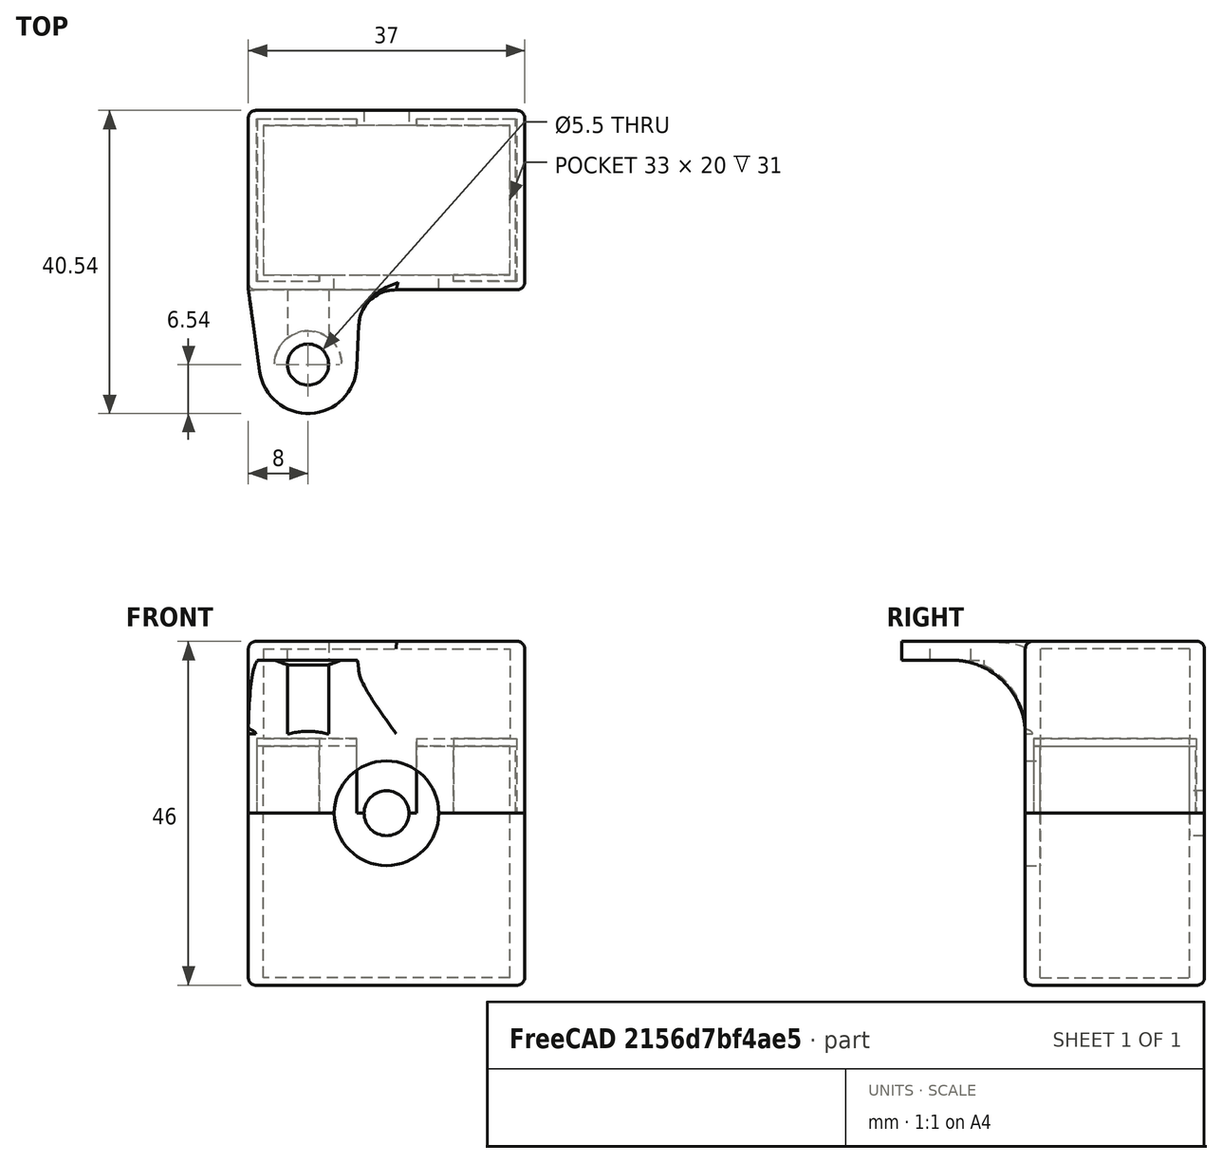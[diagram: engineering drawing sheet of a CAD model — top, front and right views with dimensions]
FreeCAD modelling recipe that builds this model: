
FCSTD DOCUMENT  (FreeCAD 1.1R)
Label: logitech-quickcam-case
License: All rights reserved
LicenseURL: https://en.wikipedia.org/wiki/All_rights_reserved
objects: Sketcher::SketchObject×13, PartDesign::Pad×7, PartDesign::Pocket×6, Part::DatumPlane×5, App::Point×4, PartDesign::Fillet×4, PartDesign::Body×2, App::FeaturePython×1, Assembly::JointGroup×1, Assembly::AssemblyObject×1
note: 79 computed .brp shape members not serialized (recipe doc carries the construction recipe); baked Part::Feature solids carry a one-line shape summary decoded from their .brp

FEATURE [App::Point] Origin001
  Role = Origin
FEATURE [Sketcher::SketchObject] Sketch
  ArcFitTolerance = 1e-06
  AttachmentSupport = -> [Origin]
  ExternalTypes = [0]
  FullyConstrained = true
  MakeInternals = false
  MapMode = 5
  sketch-geometry (12):
    g0: LineSegment StartX=0 StartY=-24 StartZ=0 EndX=0 EndY=0 EndZ=0
    g1: LineSegment StartX=0 StartY=0 StartZ=0 EndX=37 EndY=0 EndZ=0
    g2: LineSegment StartX=37 StartY=0 StartZ=0 EndX=37 EndY=-24 EndZ=0
    g3: LineSegment StartX=37 StartY=-24 StartZ=0 EndX=0 EndY=-24 EndZ=0
    g4: LineSegment StartX=2 StartY=-22 StartZ=0 EndX=2 EndY=-2 EndZ=0
    g5: LineSegment StartX=2 StartY=-2 StartZ=0 EndX=35 EndY=-2 EndZ=0
    g6: LineSegment StartX=35 StartY=-2 StartZ=0 EndX=35 EndY=-22 EndZ=0
    g7: LineSegment StartX=35 StartY=-22 StartZ=0 EndX=2 EndY=-22 EndZ=0
    g8: LineSegment [constr] StartX=0 StartY=-2 StartZ=0 EndX=2 EndY=-2 EndZ=0
    g9: LineSegment [constr] StartX=35 StartY=-2 StartZ=0 EndX=37 EndY=-2 EndZ=0
    g10: LineSegment [constr] StartX=2 StartY=-22 StartZ=0 EndX=2 EndY=-24 EndZ=0
    g11: LineSegment [constr] StartX=2 StartY=-2 StartZ=0 EndX=2 EndY=0 EndZ=0
  constraints (36):
    c: Coincident(g0,g1)
    c: Coincident(g1,g2)
    c: Coincident(g2,g3)
    c: Coincident(g3,g0)
    c: Vertical(g0)
    c: Vertical(g2)
    c: Horizontal(g1)
    c: Horizontal(g3)
    c: PointOnObject(g0,g-2)
    c: PointOnObject(g1,g-1)
    c: Coincident(g4,g5)
    c: Coincident(g5,g6)
    c: Coincident(g6,g7)
    c: Coincident(g7,g4)
    c: Vertical(g4)
    c: Vertical(g6)
    c: Horizontal(g5)
    c: Horizontal(g7)
    c: PointOnObject(g8,g0)
    c: Coincident(g8,g4)
    c: Horizontal(g8)
    c: Coincident(g9,g5)
    c: PointOnObject(g9,g2)
    c: Horizontal(g9)
    c: Equal(g8,g9)
    c: Coincident(g10,g4)
    c: PointOnObject(g10,g3)
    c: Vertical(g10)
    c: Coincident(g11,g4)
    c: PointOnObject(g11,g1)
    c: Perpendicular(g11,g1)
    c: Equal(g11,g10)
    c: Equal(g11,g8)
    c: Distance(g4,g8) = 2
    c: DistanceY(g4,g4) = 20
    c: DistanceX(g7,g7) = 33
FEATURE [PartDesign::Pad] Pad
  Direction = (0,0,1)
  Length = 23
  Length2 = 10
  Profile = -> Sketch
  ReferenceAxis = -> Sketch [N_Axis]
  Refine = true
  SideType = 0
  Suppressed = false
  Type = 0
  Type2 = 0
FEATURE [Sketcher::SketchObject] Sketch001
  ArcFitTolerance = 1e-06
  AttachmentSupport = -> [Origin]
  ExternalTypes = [0]
  FullyConstrained = true
  MakeInternals = false
  MapMode = 5
  sketch-geometry (4):
    g0: LineSegment StartX=0 StartY=0 StartZ=0 EndX=0 EndY=-24 EndZ=0
    g1: LineSegment StartX=0 StartY=-24 StartZ=0 EndX=37 EndY=-24 EndZ=0
    g2: LineSegment StartX=37 StartY=-24 StartZ=0 EndX=37 EndY=0 EndZ=0
    g3: LineSegment StartX=37 StartY=0 StartZ=0 EndX=0 EndY=0 EndZ=0
  constraints (11):
    c: Coincident(g0,g1)
    c: Coincident(g1,g2)
    c: Coincident(g2,g3)
    c: Coincident(g3,g0)
    c: Vertical(g0)
    c: Vertical(g2)
    c: Horizontal(g1)
    c: Horizontal(g3)
    c: Distance(g0,g2) = 37
    c: Distance(g1,g3) = 24
    c: Coincident(g0,g-1)
FEATURE [PartDesign::Pad] Pad001
  BaseFeature = -> Pad
  Direction = (0,0,1)
  Length = 1
  Length2 = 10
  Profile = -> Sketch001
  ReferenceAxis = -> Sketch001 [N_Axis]
  Refine = true
  SideType = 0
  Suppressed = false
  Type = 0
  Type2 = 0
FEATURE [Sketcher::SketchObject] Sketch002
  ArcFitTolerance = 1e-06
  AttachmentSupport = -> [Origin]
  ExternalTypes = [0]
  FullyConstrained = true
  MakeInternals = false
  MapMode = 5
  sketch-geometry (28):
    g0: LineSegment StartX=1.2 StartY=-22.8 StartZ=0 EndX=1.2 EndY=-1.2 EndZ=0
    g1: LineSegment [constr] StartX=1.2 StartY=-1.2 StartZ=0 EndX=35.8 EndY=-1.2 EndZ=0
    g2: LineSegment StartX=35.8 StartY=-1.2 StartZ=0 EndX=35.8 EndY=-22.8 EndZ=0
    g3: LineSegment [constr] StartX=35.8 StartY=-22.8 StartZ=0 EndX=1.2 EndY=-22.8 EndZ=0
    g4: LineSegment StartX=2 StartY=-22 StartZ=0 EndX=2 EndY=-2 EndZ=0
    g5: LineSegment [constr] StartX=2 StartY=-2 StartZ=0 EndX=35 EndY=-2 EndZ=0
    g6: LineSegment StartX=35 StartY=-2 StartZ=0 EndX=35 EndY=-22 EndZ=0
    g7: LineSegment [constr] StartX=35 StartY=-22 StartZ=0 EndX=2 EndY=-22 EndZ=0
    g8: LineSegment [constr] StartX=1.2 StartY=-2 StartZ=0 EndX=2 EndY=-2 EndZ=0
    g9: LineSegment [constr] StartX=35 StartY=-2 StartZ=0 EndX=35.8 EndY=-2 EndZ=0
    g10: LineSegment [constr] StartX=2 StartY=-22 StartZ=0 EndX=2 EndY=-22.8 EndZ=0
    g11: LineSegment [constr] StartX=2 StartY=-2 StartZ=0 EndX=2 EndY=-1.2 EndZ=0
    g12: LineSegment [constr] StartX=1.2 StartY=-1.2 StartZ=0 EndX=0 EndY=-1.2 EndZ=0
    g13: LineSegment [constr] StartX=1.2 StartY=-1.2 StartZ=0 EndX=1.2 EndY=0 EndZ=0
    g14: LineSegment StartX=14.5 StartY=-2 StartZ=0 EndX=14.5 EndY=-1.2 EndZ=0
    g15: LineSegment StartX=22.5 StartY=-1.2 StartZ=0 EndX=22.5 EndY=-2 EndZ=0
    g16: LineSegment StartX=22.5 StartY=-1.2 StartZ=0 EndX=35.8 EndY=-1.2 EndZ=0
    g17: LineSegment StartX=35 StartY=-2 StartZ=0 EndX=22.5 EndY=-2 EndZ=0
    g18: LineSegment StartX=14.5 StartY=-2 StartZ=0 EndX=2 EndY=-2 EndZ=0
    g19: LineSegment StartX=14.5 StartY=-1.2 StartZ=0 EndX=2 EndY=-1.2 EndZ=0
    g20: LineSegment StartX=2 StartY=-1.2 StartZ=0 EndX=1.2 EndY=-1.2 EndZ=0
    g21: LineSegment StartX=2 StartY=-22 StartZ=0 EndX=9.5 EndY=-22 EndZ=0
    g22: LineSegment StartX=9.5 StartY=-22 StartZ=0 EndX=9.5 EndY=-22.8 EndZ=0
    g23: LineSegment StartX=9.5 StartY=-22.8 StartZ=0 EndX=1.2 EndY=-22.8 EndZ=0
    g24: LineSegment StartX=35 StartY=-22 StartZ=0 EndX=27.5 EndY=-22 EndZ=0
    g25: LineSegment StartX=27.5 StartY=-22 StartZ=0 EndX=27.5 EndY=-22.8 EndZ=0
    g26: LineSegment [constr] StartX=9.5 StartY=-22 StartZ=0 EndX=27.5 EndY=-22 EndZ=0
    g27: LineSegment StartX=27.5 StartY=-22.8 StartZ=0 EndX=35.8 EndY=-22.8 EndZ=0
  constraints (78):
    c: Coincident(g0,g1)
    c: Coincident(g1,g2)
    c: Coincident(g2,g3)
    c: Coincident(g3,g0)
    c: Vertical(g0)
    c: Vertical(g2)
    c: Horizontal(g1)
    c: Horizontal(g3)
    c: Coincident(g4,g5)
    c: Coincident(g5,g6)
    c: Coincident(g6,g7)
    c: Coincident(g7,g4)
    c: Vertical(g4)
    c: Vertical(g6)
    c: Horizontal(g5)
    c: Horizontal(g7)
    c: PointOnObject(g8,g0)
    c: Coincident(g8,g4)
    c: Horizontal(g8)
    c: Coincident(g9,g5)
    c: PointOnObject(g9,g2)
    c: Horizontal(g9)
    c: Equal(g8,g9)
    c: Coincident(g10,g4)
    c: PointOnObject(g10,g3)
    c: Vertical(g10)
    c: Coincident(g11,g4)
    c: PointOnObject(g11,g1)
    c: Perpendicular(g11,g1)
    c: Equal(g11,g10)
    c: Equal(g11,g8)
    c: Distance(g4,g8) = 0.8
    c: DistanceY(g4,g4) = 20
    c: DistanceX(g7,g7) = 33
    c: Coincident(g12,g0)
    c: PointOnObject(g12,g-2)
    c: Horizontal(g12)
    c: Coincident(g13,g0)
    c: Vertical(g13)
    c: Equal(g12,g13)
    c: PointOnObject(g13,g-1)
    c: DistanceY(g13,g13) = 1.2
    c: PointOnObject(g14,g5)
    c: PointOnObject(g14,g1)
    c: PointOnObject(g15,g1)
    c: PointOnObject(g15,g5)
    c: Vertical(g15)
    c: Coincident(g16,g15)
    c: Coincident(g16,g1)
    c: Coincident(g17,g5)
    c: Coincident(g17,g15)
    c: Coincident(g18,g14)
    c: Coincident(g18,g4)
    c: Coincident(g19,g14)
    c: Coincident(g19,g11)
    c: Perpendicular(g18,g14)
    c: DistanceX(g14,g15) = 8
    c: Coincident(g20,g11)
    c: Coincident(g20,g0)
    c: Coincident(g21,g4)
    c: Coincident(g21,g22)
    c: Vertical(g22)
    c: Coincident(g22,g23)
    c: Coincident(g23,g0)
    c: Coincident(g24,g6)
    c: Coincident(g24,g25)
    c: Coincident(g26,g21)
    c: Coincident(g26,g24)
    c: Horizontal(g26)
    c: DistanceX(g26,g26) = 18
    c: Perpendicular(g25,g24)
    c: Perpendicular(g6,g24)
    c: Horizontal(g25,g22)
    c: Horizontal(g22,g2)
    c: Equal(g18,g17)
    c: Equal(g21,g24)
    c: Coincident(g27,g25)
    c: Coincident(g27,g2)
FEATURE [Part::DatumPlane] DatumPlane
  AttachmentOffset = pos=(0,0,0) rot=(0,1,0;1.5708rad)
  AttachmentSupport = -> [Pad001]
  MapMode = 7
  Placement = pos=(2,-2,23) rot=(1,0,0;1.5708rad)
FEATURE [Sketcher::SketchObject] Sketch003
  ArcFitTolerance = 1e-06
  AttachmentSupport = -> [DatumPlane]
  ExternalTypes = [0]
  FullyConstrained = true
  MakeInternals = false
  MapMode = 5
  Placement = pos=(2,-2,23) rot=(1,0,0;1.5708rad)
  sketch-geometry (1):
    g0: Circle CenterX=16.5 CenterY=0 CenterZ=0 NormalX=0 NormalY=0 NormalZ=1 AngleXU=0 Radius=3
  constraints (3):
    c: PointOnObject(g0,g-1)
    c: Diameter(g0) = 6
    c: DistanceX(g-1,g0) = 16.5
FEATURE [PartDesign::Pocket] Pocket
  BaseFeature = -> Pad001
  Direction = (0,1,-2e-16)
  Length = 5
  Length2 = 5
  Profile = -> Sketch003
  ReferenceAxis = -> Sketch003 [N_Axis]
  Refine = true
  SideType = 2
  Suppressed = false
  Type = 0
  Type2 = 0
FEATURE [Part::DatumPlane] DatumPlane001
  AttachmentOffset = pos=(0,0,0) rot=(0,1,0;1.5708rad)
  AttachmentSupport = -> [Pad001]
  MapMode = 7
  Placement = pos=(35,-22,23) rot=(0,0.707107,0.707107;3.14159rad)
FEATURE [Sketcher::SketchObject] Sketch005
  ArcFitTolerance = 1e-06
  AttachmentSupport = -> [DatumPlane001]
  ExternalTypes = [0]
  FullyConstrained = true
  MakeInternals = false
  MapMode = 5
  Placement = pos=(35,-22,23) rot=(0,0.707107,0.707107;3.14159rad)
  sketch-geometry (1):
    g0: Circle CenterX=16.5 CenterY=0 CenterZ=0 NormalX=0 NormalY=0 NormalZ=1 AngleXU=0 Radius=7
  constraints (3):
    c: Diameter(g0) = 14
    c: PointOnObject(g0,g-1)
    c: DistanceX(g-1,g0) = 16.5
FEATURE [PartDesign::Pocket] Pocket001
  BaseFeature = -> Pocket
  Direction = (0,-1,2e-16)
  Length = 5
  Length2 = 5
  Profile = -> Sketch005
  ReferenceAxis = -> Sketch005 [N_Axis]
  Refine = true
  SideType = 2
  Suppressed = false
  Type = 0
  Type2 = 0
FEATURE [PartDesign::Pad] Pad002
  BaseFeature = -> Pocket001
  Direction = (0,0,1)
  Length = 32
  Length2 = 10
  Profile = -> Sketch002
  ReferenceAxis = -> Sketch002 [N_Axis]
  Refine = true
  SideType = 0
  Suppressed = false
  Type = 0
  Type2 = 0
FEATURE [App::Point] Origin005
  Role = Origin
FEATURE [Sketcher::SketchObject] Sketch006
  ArcFitTolerance = 1e-06
  AttachmentOffset = pos=(0,0,0) rot=(1,0,0;3.14159rad)
  ExternalTypes = [0]
  FullyConstrained = true
  MakeInternals = false
  MapMode = 5
  Placement = pos=(0,0,23) rot=(0,0,1;0rad)
  sketch-geometry (28):
    g0: LineSegment StartX=1.1 StartY=-22.9 StartZ=0 EndX=1.1 EndY=-1.1 EndZ=0
    g1: LineSegment [constr] StartX=1.1 StartY=-1.1 StartZ=0 EndX=35.9 EndY=-1.1 EndZ=0
    g2: LineSegment StartX=35.9 StartY=-1.1 StartZ=0 EndX=35.9 EndY=-22.9 EndZ=0
    g3: LineSegment [constr] StartX=35.9 StartY=-22.9 StartZ=0 EndX=1.1 EndY=-22.9 EndZ=0
    g4: LineSegment StartX=2 StartY=-22 StartZ=0 EndX=2 EndY=-2 EndZ=0
    g5: LineSegment [constr] StartX=2 StartY=-2 StartZ=0 EndX=35 EndY=-2 EndZ=0
    g6: LineSegment StartX=35 StartY=-2 StartZ=0 EndX=35 EndY=-22 EndZ=0
    g7: LineSegment [constr] StartX=35 StartY=-22 StartZ=0 EndX=2 EndY=-22 EndZ=0
    g8: LineSegment [constr] StartX=1.1 StartY=-2 StartZ=0 EndX=2 EndY=-2 EndZ=0
    g9: LineSegment [constr] StartX=35 StartY=-2 StartZ=0 EndX=35.9 EndY=-2 EndZ=0
    g10: LineSegment [constr] StartX=2 StartY=-22 StartZ=0 EndX=2 EndY=-22.9 EndZ=0
    g11: LineSegment [constr] StartX=2 StartY=-2 StartZ=0 EndX=2 EndY=-1.1 EndZ=0
    g12: LineSegment [constr] StartX=1.1 StartY=-1.1 StartZ=0 EndX=0 EndY=-1.1 EndZ=0
    g13: LineSegment [constr] StartX=1.1 StartY=-1.1 StartZ=0 EndX=1.1 EndY=0 EndZ=0
    g14: LineSegment StartX=14.5 StartY=-2 StartZ=0 EndX=14.5 EndY=-1.1 EndZ=0
    g15: LineSegment StartX=22.5 StartY=-1.1 StartZ=0 EndX=22.5 EndY=-2 EndZ=0
    g16: LineSegment StartX=22.5 StartY=-1.1 StartZ=0 EndX=35.9 EndY=-1.1 EndZ=0
    g17: LineSegment StartX=35 StartY=-2 StartZ=0 EndX=22.5 EndY=-2 EndZ=0
    g18: LineSegment StartX=14.5 StartY=-2 StartZ=0 EndX=2 EndY=-2 EndZ=0
    g19: LineSegment StartX=14.5 StartY=-1.1 StartZ=0 EndX=2 EndY=-1.1 EndZ=0
    g20: LineSegment StartX=2 StartY=-1.1 StartZ=0 EndX=1.1 EndY=-1.1 EndZ=0
    g21: LineSegment StartX=2 StartY=-22 StartZ=0 EndX=9.5 EndY=-22 EndZ=0
    g22: LineSegment StartX=9.5 StartY=-22 StartZ=0 EndX=9.5 EndY=-22.9 EndZ=0
    g23: LineSegment StartX=9.5 StartY=-22.9 StartZ=0 EndX=1.1 EndY=-22.9 EndZ=0
    g24: LineSegment StartX=35 StartY=-22 StartZ=0 EndX=27.5 EndY=-22 EndZ=0
    g25: LineSegment StartX=27.5 StartY=-22 StartZ=0 EndX=27.5 EndY=-22.9 EndZ=0
    g26: LineSegment [constr] StartX=9.5 StartY=-22 StartZ=0 EndX=27.5 EndY=-22 EndZ=0
    g27: LineSegment StartX=27.5 StartY=-22.9 StartZ=0 EndX=35.9 EndY=-22.9 EndZ=0
  constraints (78):
    c: Coincident(g0,g1)
    c: Coincident(g1,g2)
    c: Coincident(g2,g3)
    c: Coincident(g3,g0)
    c: Vertical(g0)
    c: Vertical(g2)
    c: Horizontal(g1)
    c: Horizontal(g3)
    c: Coincident(g4,g5)
    c: Coincident(g5,g6)
    c: Coincident(g6,g7)
    c: Coincident(g7,g4)
    c: Vertical(g4)
    c: Vertical(g6)
    c: Horizontal(g5)
    c: Horizontal(g7)
    c: PointOnObject(g8,g0)
    c: Coincident(g8,g4)
    c: Horizontal(g8)
    c: Coincident(g9,g5)
    c: PointOnObject(g9,g2)
    c: Horizontal(g9)
    c: Equal(g8,g9)
    c: Coincident(g10,g4)
    c: PointOnObject(g10,g3)
    c: Vertical(g10)
    c: Coincident(g11,g4)
    c: PointOnObject(g11,g1)
    c: Perpendicular(g11,g1)
    c: Equal(g11,g10)
    c: Equal(g11,g8)
    c: Distance(g4,g8) = 0.9
    c: DistanceY(g4,g4) = 20
    c: DistanceX(g7,g7) = 33
    c: Coincident(g12,g0)
    c: PointOnObject(g12,g-2)
    c: Horizontal(g12)
    c: Coincident(g13,g0)
    c: Vertical(g13)
    c: Equal(g12,g13)
    c: PointOnObject(g13,g-1)
    c: DistanceY(g13,g13) = 1.1
    c: PointOnObject(g14,g5)
    c: PointOnObject(g14,g1)
    c: PointOnObject(g15,g1)
    c: PointOnObject(g15,g5)
    c: Vertical(g15)
    c: Coincident(g16,g15)
    c: Coincident(g16,g1)
    c: Coincident(g17,g5)
    c: Coincident(g17,g15)
    c: Coincident(g18,g14)
    c: Coincident(g18,g4)
    c: Coincident(g19,g14)
    c: Coincident(g19,g11)
    c: Perpendicular(g18,g14)
    c: DistanceX(g14,g15) = 8
    c: Coincident(g20,g11)
    c: Coincident(g20,g0)
    c: Coincident(g21,g4)
    c: Coincident(g21,g22)
    c: Vertical(g22)
    c: Coincident(g22,g23)
    c: Coincident(g23,g0)
    c: Coincident(g24,g6)
    c: Coincident(g24,g25)
    c: Coincident(g26,g21)
    c: Coincident(g26,g24)
    c: Horizontal(g26)
    c: DistanceX(g26,g26) = 18
    c: Perpendicular(g25,g24)
    c: Perpendicular(g6,g24)
    c: Horizontal(g25,g22)
    c: Horizontal(g22,g2)
    c: Equal(g18,g17)
    c: Equal(g21,g24)
    c: Coincident(g27,g25)
    c: Coincident(g27,g2)
FEATURE [App::Point] Origin007
  Role = Origin
FEATURE [Sketcher::SketchObject] Sketch007
  ArcFitTolerance = 1e-06
  AttachmentSupport = -> [Origin006]
  ExternalTypes = [0]
  FullyConstrained = true
  MakeInternals = false
  MapMode = 5
  sketch-geometry (12):
    g0: LineSegment StartX=0 StartY=-24 StartZ=0 EndX=0 EndY=0 EndZ=0
    g1: LineSegment StartX=0 StartY=0 StartZ=0 EndX=37 EndY=0 EndZ=0
    g2: LineSegment StartX=37 StartY=0 StartZ=0 EndX=37 EndY=-24 EndZ=0
    g3: LineSegment StartX=37 StartY=-24 StartZ=0 EndX=0 EndY=-24 EndZ=0
    g4: LineSegment StartX=2 StartY=-22 StartZ=0 EndX=2 EndY=-2 EndZ=0
    g5: LineSegment StartX=2 StartY=-2 StartZ=0 EndX=35 EndY=-2 EndZ=0
    g6: LineSegment StartX=35 StartY=-2 StartZ=0 EndX=35 EndY=-22 EndZ=0
    g7: LineSegment StartX=35 StartY=-22 StartZ=0 EndX=2 EndY=-22 EndZ=0
    g8: LineSegment [constr] StartX=0 StartY=-2 StartZ=0 EndX=2 EndY=-2 EndZ=0
    g9: LineSegment [constr] StartX=35 StartY=-2 StartZ=0 EndX=37 EndY=-2 EndZ=0
    g10: LineSegment [constr] StartX=2 StartY=-22 StartZ=0 EndX=2 EndY=-24 EndZ=0
    g11: LineSegment [constr] StartX=2 StartY=-2 StartZ=0 EndX=2 EndY=0 EndZ=0
  constraints (36):
    c: Coincident(g0,g1)
    c: Coincident(g1,g2)
    c: Coincident(g2,g3)
    c: Coincident(g3,g0)
    c: Vertical(g0)
    c: Vertical(g2)
    c: Horizontal(g1)
    c: Horizontal(g3)
    c: PointOnObject(g0,g-2)
    c: PointOnObject(g1,g-1)
    c: Coincident(g4,g5)
    c: Coincident(g5,g6)
    c: Coincident(g6,g7)
    c: Coincident(g7,g4)
    c: Vertical(g4)
    c: Vertical(g6)
    c: Horizontal(g5)
    c: Horizontal(g7)
    c: PointOnObject(g8,g0)
    c: Coincident(g8,g4)
    c: Horizontal(g8)
    c: Coincident(g9,g5)
    c: PointOnObject(g9,g2)
    c: Horizontal(g9)
    c: Equal(g8,g9)
    c: Coincident(g10,g4)
    c: PointOnObject(g10,g3)
    c: Vertical(g10)
    c: Coincident(g11,g4)
    c: PointOnObject(g11,g1)
    c: Perpendicular(g11,g1)
    c: Equal(g11,g10)
    c: Equal(g11,g8)
    c: Distance(g4,g8) = 2
    c: DistanceY(g4,g4) = 20
    c: DistanceX(g7,g7) = 33
FEATURE [PartDesign::Pad] Pad003
  Direction = (0,0,1)
  Length = 23
  Length2 = 10
  Profile = -> Sketch007
  ReferenceAxis = -> Sketch007 [N_Axis]
  Refine = true
  SideType = 0
  Suppressed = false
  Type = 0
  Type2 = 0
FEATURE [Sketcher::SketchObject] Sketch008
  ArcFitTolerance = 1e-06
  AttachmentSupport = -> [Origin006]
  ExternalTypes = [0]
  FullyConstrained = true
  MakeInternals = false
  MapMode = 5
  sketch-geometry (4):
    g0: LineSegment StartX=0 StartY=0 StartZ=0 EndX=0 EndY=-24 EndZ=0
    g1: LineSegment StartX=0 StartY=-24 StartZ=0 EndX=37 EndY=-24 EndZ=0
    g2: LineSegment StartX=37 StartY=-24 StartZ=0 EndX=37 EndY=0 EndZ=0
    g3: LineSegment StartX=37 StartY=0 StartZ=0 EndX=0 EndY=0 EndZ=0
  constraints (11):
    c: Coincident(g0,g1)
    c: Coincident(g1,g2)
    c: Coincident(g2,g3)
    c: Coincident(g3,g0)
    c: Vertical(g0)
    c: Vertical(g2)
    c: Horizontal(g1)
    c: Horizontal(g3)
    c: Distance(g0,g2) = 37
    c: Distance(g1,g3) = 24
    c: Coincident(g0,g-1)
FEATURE [PartDesign::Pad] Pad004
  BaseFeature = -> Pad003
  Direction = (0,0,1)
  Length = 1
  Length2 = 10
  Profile = -> Sketch008
  ReferenceAxis = -> Sketch008 [N_Axis]
  Refine = true
  SideType = 0
  Suppressed = false
  Type = 0
  Type2 = 0
FEATURE [Part::DatumPlane] DatumPlane002
  AttachmentOffset = pos=(0,0,0) rot=(0,1,0;1.5708rad)
  AttachmentSupport = -> [Pad004]
  MapMode = 7
  Placement = pos=(2,-2,23) rot=(1,0,0;1.5708rad)
FEATURE [Part::DatumPlane] DatumPlane003
  AttachmentOffset = pos=(0,0,0) rot=(0,1,0;1.5708rad)
  AttachmentSupport = -> [Pad004]
  MapMode = 7
  Placement = pos=(35,-22,23) rot=(0,0.707107,0.707107;3.14159rad)
FEATURE [Sketcher::SketchObject] Sketch009
  ArcFitTolerance = 1e-06
  AttachmentSupport = -> [Origin006]
  ExternalTypes = [0]
  FullyConstrained = true
  MakeInternals = false
  MapMode = 5
  sketch-geometry (28):
    g0: LineSegment StartX=1.2 StartY=-22.8 StartZ=0 EndX=1.2 EndY=-1.2 EndZ=0
    g1: LineSegment [constr] StartX=1.2 StartY=-1.2 StartZ=0 EndX=35.8 EndY=-1.2 EndZ=0
    g2: LineSegment StartX=35.8 StartY=-1.2 StartZ=0 EndX=35.8 EndY=-22.8 EndZ=0
    g3: LineSegment [constr] StartX=35.8 StartY=-22.8 StartZ=0 EndX=1.2 EndY=-22.8 EndZ=0
    g4: LineSegment StartX=2 StartY=-22 StartZ=0 EndX=2 EndY=-2 EndZ=0
    g5: LineSegment [constr] StartX=2 StartY=-2 StartZ=0 EndX=35 EndY=-2 EndZ=0
    g6: LineSegment StartX=35 StartY=-2 StartZ=0 EndX=35 EndY=-22 EndZ=0
    g7: LineSegment [constr] StartX=35 StartY=-22 StartZ=0 EndX=2 EndY=-22 EndZ=0
    g8: LineSegment [constr] StartX=1.2 StartY=-2 StartZ=0 EndX=2 EndY=-2 EndZ=0
    g9: LineSegment [constr] StartX=35 StartY=-2 StartZ=0 EndX=35.8 EndY=-2 EndZ=0
    g10: LineSegment [constr] StartX=2 StartY=-22 StartZ=0 EndX=2 EndY=-22.8 EndZ=0
    g11: LineSegment [constr] StartX=2 StartY=-2 StartZ=0 EndX=2 EndY=-1.2 EndZ=0
    g12: LineSegment [constr] StartX=1.2 StartY=-1.2 StartZ=0 EndX=0 EndY=-1.2 EndZ=0
    g13: LineSegment [constr] StartX=1.2 StartY=-1.2 StartZ=0 EndX=1.2 EndY=0 EndZ=0
    g14: LineSegment StartX=14.5 StartY=-2 StartZ=0 EndX=14.5 EndY=-1.2 EndZ=0
    g15: LineSegment StartX=22.5 StartY=-1.2 StartZ=0 EndX=22.5 EndY=-2 EndZ=0
    g16: LineSegment StartX=22.5 StartY=-1.2 StartZ=0 EndX=35.8 EndY=-1.2 EndZ=0
    g17: LineSegment StartX=35 StartY=-2 StartZ=0 EndX=22.5 EndY=-2 EndZ=0
    g18: LineSegment StartX=14.5 StartY=-2 StartZ=0 EndX=2 EndY=-2 EndZ=0
    g19: LineSegment StartX=14.5 StartY=-1.2 StartZ=0 EndX=2 EndY=-1.2 EndZ=0
    g20: LineSegment StartX=2 StartY=-1.2 StartZ=0 EndX=1.2 EndY=-1.2 EndZ=0
    g21: LineSegment StartX=2 StartY=-22 StartZ=0 EndX=9.5 EndY=-22 EndZ=0
    g22: LineSegment StartX=9.5 StartY=-22 StartZ=0 EndX=9.5 EndY=-22.8 EndZ=0
    g23: LineSegment StartX=9.5 StartY=-22.8 StartZ=0 EndX=1.2 EndY=-22.8 EndZ=0
    g24: LineSegment StartX=35 StartY=-22 StartZ=0 EndX=27.5 EndY=-22 EndZ=0
    g25: LineSegment StartX=27.5 StartY=-22 StartZ=0 EndX=27.5 EndY=-22.8 EndZ=0
    g26: LineSegment [constr] StartX=9.5 StartY=-22 StartZ=0 EndX=27.5 EndY=-22 EndZ=0
    g27: LineSegment StartX=27.5 StartY=-22.8 StartZ=0 EndX=35.8 EndY=-22.8 EndZ=0
  constraints (78):
    c: Coincident(g0,g1)
    c: Coincident(g1,g2)
    c: Coincident(g2,g3)
    c: Coincident(g3,g0)
    c: Vertical(g0)
    c: Vertical(g2)
    c: Horizontal(g1)
    c: Horizontal(g3)
    c: Coincident(g4,g5)
    c: Coincident(g5,g6)
    c: Coincident(g6,g7)
    c: Coincident(g7,g4)
    c: Vertical(g4)
    c: Vertical(g6)
    c: Horizontal(g5)
    c: Horizontal(g7)
    c: PointOnObject(g8,g0)
    c: Coincident(g8,g4)
    c: Horizontal(g8)
    c: Coincident(g9,g5)
    c: PointOnObject(g9,g2)
    c: Horizontal(g9)
    c: Equal(g8,g9)
    c: Coincident(g10,g4)
    c: PointOnObject(g10,g3)
    c: Vertical(g10)
    c: Coincident(g11,g4)
    c: PointOnObject(g11,g1)
    c: Perpendicular(g11,g1)
    c: Equal(g11,g10)
    c: Equal(g11,g8)
    c: Distance(g4,g8) = 0.8
    c: DistanceY(g4,g4) = 20
    c: DistanceX(g7,g7) = 33
    c: Coincident(g12,g0)
    c: PointOnObject(g12,g-2)
    c: Horizontal(g12)
    c: Coincident(g13,g0)
    c: Vertical(g13)
    c: Equal(g12,g13)
    c: PointOnObject(g13,g-1)
    c: DistanceY(g13,g13) = 1.2
    c: PointOnObject(g14,g5)
    c: PointOnObject(g14,g1)
    c: PointOnObject(g15,g1)
    c: PointOnObject(g15,g5)
    c: Vertical(g15)
    c: Coincident(g16,g15)
    c: Coincident(g16,g1)
    c: Coincident(g17,g5)
    c: Coincident(g17,g15)
    c: Coincident(g18,g14)
    c: Coincident(g18,g4)
    c: Coincident(g19,g14)
    c: Coincident(g19,g11)
    c: Perpendicular(g18,g14)
    c: DistanceX(g14,g15) = 8
    c: Coincident(g20,g11)
    c: Coincident(g20,g0)
    c: Coincident(g21,g4)
    c: Coincident(g21,g22)
    c: Vertical(g22)
    c: Coincident(g22,g23)
    c: Coincident(g23,g0)
    c: Coincident(g24,g6)
    c: Coincident(g24,g25)
    c: Coincident(g26,g21)
    c: Coincident(g26,g24)
    c: Horizontal(g26)
    c: DistanceX(g26,g26) = 18
    c: Perpendicular(g25,g24)
    c: Perpendicular(g6,g24)
    c: Horizontal(g25,g22)
    c: Horizontal(g22,g2)
    c: Equal(g18,g17)
    c: Equal(g21,g24)
    c: Coincident(g27,g25)
    c: Coincident(g27,g2)
FEATURE [Sketcher::SketchObject] Sketch010
  ArcFitTolerance = 1e-06
  AttachmentSupport = -> [DatumPlane002]
  ExternalTypes = [0]
  FullyConstrained = true
  MakeInternals = false
  MapMode = 5
  Placement = pos=(2,-2,23) rot=(1,0,0;1.5708rad)
  sketch-geometry (1):
    g0: Circle CenterX=16.5 CenterY=0 CenterZ=0 NormalX=0 NormalY=0 NormalZ=1 AngleXU=0 Radius=3
  constraints (3):
    c: PointOnObject(g0,g-1)
    c: Diameter(g0) = 6
    c: DistanceX(g-1,g0) = 16.5
FEATURE [PartDesign::Pocket] Pocket002
  BaseFeature = -> Pad004
  Direction = (0,1,-2e-16)
  Length = 5
  Length2 = 5
  Profile = -> Sketch010
  ReferenceAxis = -> Sketch010 [N_Axis]
  Refine = true
  SideType = 2
  Suppressed = false
  Type = 0
  Type2 = 0
FEATURE [Sketcher::SketchObject] Sketch011
  ArcFitTolerance = 1e-06
  AttachmentSupport = -> [DatumPlane003]
  ExternalTypes = [0]
  FullyConstrained = true
  MakeInternals = false
  MapMode = 5
  Placement = pos=(35,-22,23) rot=(0,0.707107,0.707107;3.14159rad)
  sketch-geometry (1):
    g0: Circle CenterX=16.5 CenterY=0 CenterZ=0 NormalX=0 NormalY=0 NormalZ=1 AngleXU=0 Radius=7
  constraints (3):
    c: Diameter(g0) = 14
    c: PointOnObject(g0,g-1)
    c: DistanceX(g-1,g0) = 16.5
FEATURE [PartDesign::Pocket] Pocket003
  BaseFeature = -> Pocket002
  Direction = (0,-1,2e-16)
  Length = 5
  Length2 = 5
  Profile = -> Sketch011
  ReferenceAxis = -> Sketch011 [N_Axis]
  Refine = true
  SideType = 2
  Suppressed = false
  Type = 0
  Type2 = 0
FEATURE [PartDesign::Pad] Pad005
  BaseFeature = -> Pocket003
  Direction = (0,0,1)
  Length = 27
  Length2 = 10
  Profile = -> Sketch009
  ReferenceAxis = -> Sketch009 [N_Axis]
  Refine = true
  SideType = 0
  Suppressed = false
  Type = 0
  Type2 = 0
FEATURE [PartDesign::Pocket] Pocket004
  BaseFeature = -> Pad005
  Direction = (0,0,-1)
  Length = 10
  Length2 = 5
  Profile = -> Sketch006
  ReferenceAxis = -> Sketch006 [N_Axis]
  Refine = true
  SideType = 2
  Suppressed = false
  Type = 0
  Type2 = 0
FEATURE [App::Point] Origin009
  Role = Origin
FEATURE [App::FeaturePython] Joint  label="Fixed"  # Assembly joint (typed FeaturePython)
  AngleMax = 0
  AngleMin = 0
  Detach1 = false
  Detach2 = false
  Distance = 0
  Distance2 = 0
  EnableAngleMax = false
  EnableAngleMin = false
  EnableLengthMax = false
  EnableLengthMin = false
  JointType = 0 (Fixed)
  LengthMax = 0
  LengthMin = 0
  Placement1 = pos=(31.25,-22,18) rot=(-0.707107,0,0.707107;3.14159rad)
  Placement2 = pos=(0,-12,23) rot=(0.57735,0.57735,0.57735;4.18879rad)
  Reference1 = -> Assembly [Body001.?Edge92,Body001.?Edge92]
  Reference2 = -> Assembly [Body.?Edge14,Body.?Edge14]
  Suppressed = false
FEATURE [Assembly::JointGroup] Joints
  Group = -> [Joint]
FEATURE [PartDesign::Fillet] Fillet002
  Base = -> Pad002 [Edge29,Edge27,Edge28,Edge25,Edge49,Edge46,Edge26,Edge48]
  BaseFeature = -> Pad002
  Radius = 0.999
  Refine = true
  SupportTransform = false
  Suppressed = false
  UseAllEdges = false
FEATURE [PartDesign::Body] Body  label="free-side"
  AllowCompound = false
  Group = -> [Sketch,Pad,Sketch001,Pad001,Sketch003,Pocket,Sketch002,Sketch005,Pocket001,Pad002,DatumPlane,DatumPlane001,Fillet002]
  Origin = -> Origin
  Tip = -> Fillet002
FEATURE [Part::DatumPlane] DatumPlane005
  AttachmentOffset = pos=(0,0,0) rot=(-0.57735,0.57735,0.57735;2.0944rad)
  AttachmentSupport = -> [Pocket004]
  MapMode = 7
  Placement = pos=(37,-24,0) rot=(0,0,1;3.14159rad)
FEATURE [Sketcher::SketchObject] Sketch013
  ArcFitTolerance = 1e-06
  AttachmentSupport = -> [DatumPlane005]
  ExternalTypes = [0]
  FullyConstrained = true
  MakeInternals = false
  MapMode = 5
  Placement = pos=(37,-24,0) rot=(0,0,1;3.14159rad)
  sketch-geometry (7):
    g0: ArcOfCircle CenterX=8 CenterY=10 CenterZ=0 NormalX=0 NormalY=0 NormalZ=1 AngleXU=0 Radius=6.53503 StartAngle=0.0457794 EndAngle=3.00239
    g1: Circle CenterX=8 CenterY=10 CenterZ=0 NormalX=0 NormalY=0 NormalZ=1 AngleXU=0 Radius=2.75
    g2: LineSegment StartX=1.52819 StartY=10.9068 StartZ=0 EndX=-2e-16 EndY=0 EndZ=0
    g3: LineSegment StartX=14.5282 StartY=10.2991 StartZ=0 EndX=15 EndY=0 EndZ=0
    g4: LineSegment StartX=-2e-16 StartY=0 StartZ=0 EndX=15 EndY=0 EndZ=0
    g5: LineSegment [constr] StartX=1.52819 StartY=10.9068 StartZ=0 EndX=11.304 EndY=80.6778 EndZ=0
    g6: LineSegment [constr] StartX=14.5282 StartY=10.2991 StartZ=0 EndX=11.304 EndY=80.6778 EndZ=0
  constraints (17):
    c: Coincident(g1,g0)
    c: Diameter(g1) = 5.5
    c: DistanceX(g0,g0) = 13
    c: Coincident(g2,g0)
    c: Coincident(g3,g0)
    c: PointOnObject(g3,g-1)
    c: Coincident(g4,g2)
    c: Coincident(g4,g3)
    c: Distance(g0,g-2) = 8
    c: Coincident(g2,g-1)
    c: Distance(g0,g-1) = 10
    c: Tangent(g6,g0) = -1.5708
    c: Parallel(g6,g3)
    c: Parallel(g2,g5)
    c: Tangent(g5,g0) = 1.5708
    c: DistanceX(g4,g4) = 15
    c: Coincident(g5,g6)
FEATURE [PartDesign::Pad] Pad006
  BaseFeature = -> Pocket004
  Direction = (0,0,1)
  Length = 2.5
  Length2 = 10
  Profile = -> Sketch013
  ReferenceAxis = -> Sketch013 [N_Axis]
  Refine = true
  SideType = 0
  Suppressed = false
  Type = 0
  Type2 = 0
FEATURE [PartDesign::Fillet] Fillet
  Base = -> Pad006 [Edge70]
  BaseFeature = -> Pad006
  Radius = 9.9
  Refine = true
  SupportTransform = false
  Suppressed = false
  UseAllEdges = false
FEATURE [PartDesign::Fillet] Fillet003
  Base = -> Fillet [Edge1,Edge16,Edge15,Edge51,Edge11,Edge9,Edge50,Edge49]
  BaseFeature = -> Fillet
  Radius = 1
  Refine = true
  SupportTransform = false
  Suppressed = false
  UseAllEdges = false
FEATURE [PartDesign::Fillet] Fillet004
  Base = -> Fillet003 [Edge7]
  BaseFeature = -> Fillet003
  Radius = 5
  Refine = true
  SupportTransform = false
  Suppressed = false
  UseAllEdges = false
FEATURE [Sketcher::SketchObject] Sketch014
  ArcFitTolerance = 1e-06
  AttachmentOffset = pos=(0,0,2.5) rot=(0,0,1;0rad)
  AttachmentSupport = -> [DatumPlane005]
  ExternalTypes = [0]
  FullyConstrained = true
  MakeInternals = false
  MapMode = 5
  Placement = pos=(37,-24,2.5) rot=(0,0,1;3.14159rad)
  sketch-geometry (1):
    g0: Circle CenterX=8 CenterY=10 CenterZ=0 NormalX=0 NormalY=0 NormalZ=1 AngleXU=0 Radius=4.5
  constraints (3):
    c: Distance(g0,g-1) = 10
    c: DistanceX(g-1,g0) = 8
    c: Diameter(g0) = 9
FEATURE [PartDesign::Pocket] Pocket005
  BaseFeature = -> Fillet004
  Direction = (0,0,-1)
  Length = 5
  Length2 = 5
  Profile = -> Sketch014
  ReferenceAxis = -> Sketch014 [N_Axis]
  Refine = true
  Reversed = true
  SideType = 0
  Suppressed = false
  Type = 0
  Type2 = 0
FEATURE [PartDesign::Body] Body001  label="bracket-side"
  AllowCompound = false
  Group = -> [Sketch007,Pad003,Sketch008,Pad004,Sketch010,Pocket002,Sketch009,Sketch011,Pocket003,Pad005,DatumPlane002,DatumPlane003,Sketch006,Pocket004,Sketch013,Pad006,DatumPlane005,Fillet,Fillet003,Fillet004,Sketch014,Pocket005]
  Origin = -> Origin006
  Placement = pos=(37,1.8e-15,46) rot=(0,1,0;3.14159rad)
  Tip = -> Pocket005
FEATURE [Assembly::AssemblyObject] Assembly
  Group = -> [Joints,Body001,Body,Joint]
  Origin = -> Origin008
  Type = Assembly
